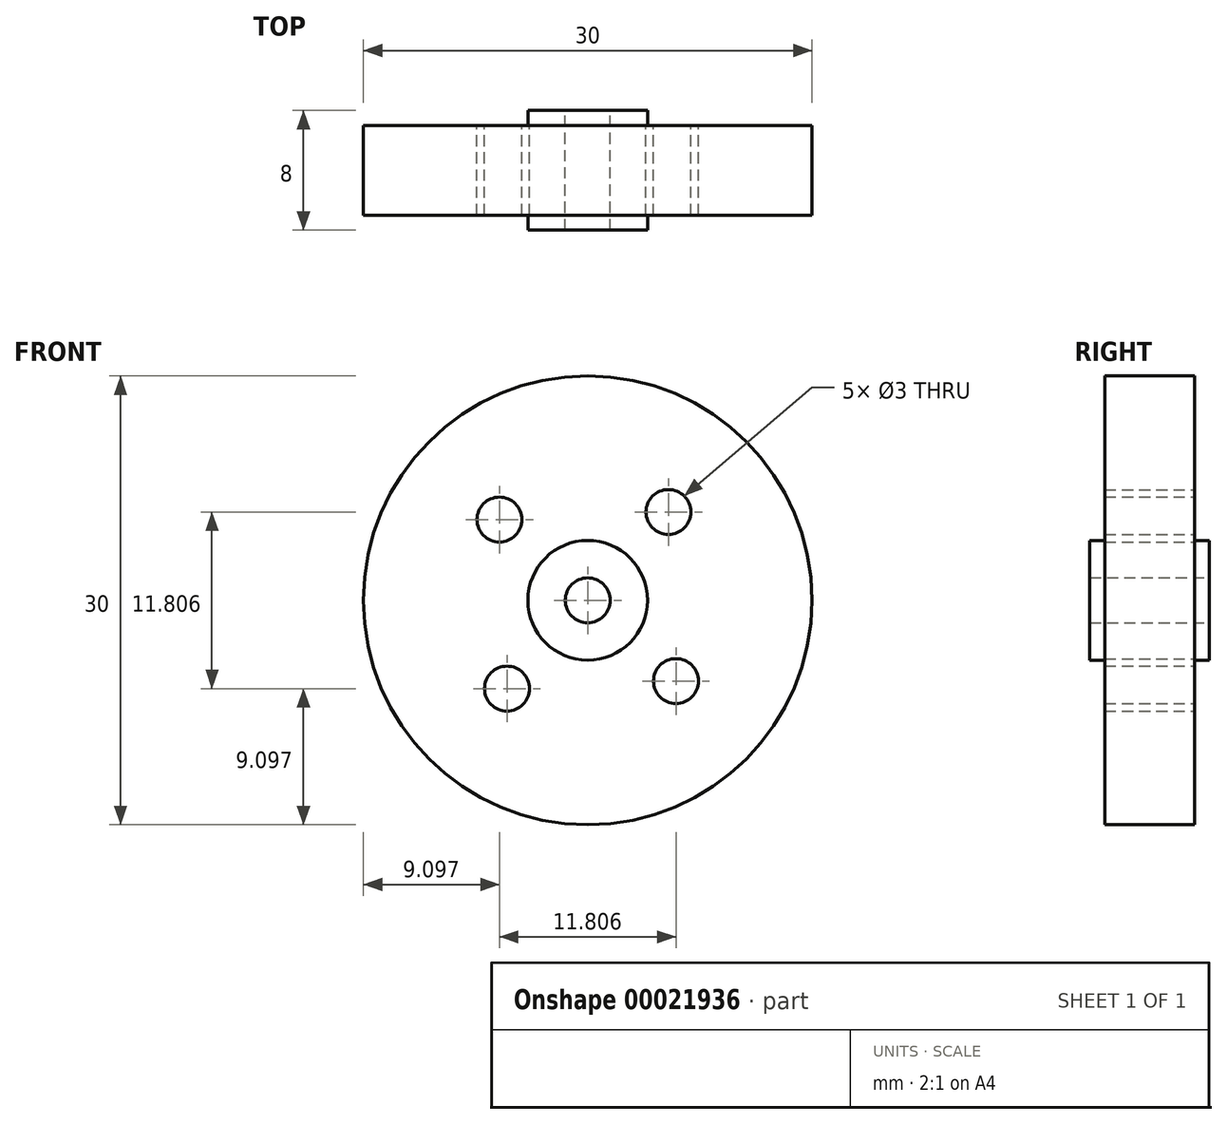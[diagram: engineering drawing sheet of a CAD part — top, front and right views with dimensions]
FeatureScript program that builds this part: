
annotation { "Feature Type Name" : "Feature", "Feature Type Description" : "" }
export const myFeature = defineFeature(function(context is Context, id is Id, definition is map)
    precondition{}
    {
        {
            var Q0;
            Q0=qCreatedBy(makeId("Front.planeOp"),FACE);
            var sketch = newSketch(context, id + "F0", { "sketchPlane" : qUnion([Q0])});
            skCircle(sketch, "E0", {"center": v(0, 0) * mm, "radius": 15 * mm});
            skCircle(sketch, "E1", {"center": v(0, 0) * mm, "radius": 1.5 * mm});
            skCircle(sketch, "E2", {"center": v(0, 0) * mm, "radius": 4 * mm});
            skCircle(sketch, "E3", {"center": v(-5.9, 5.4) * mm, "radius": 1.5 * mm});
            skCircle(sketch, "E4.1.0", {"center": v(-5.4, -5.9) * mm, "radius": 1.5 * mm});
            skCircle(sketch, "E4.2.0", {"center": v(5.9, -5.4) * mm, "radius": 1.5 * mm});
            skCircle(sketch, "E4.3.0", {"center": v(5.4, 5.9) * mm, "radius": 1.5 * mm});
            skSolve(sketch);
        }
        {
            var Q0;
            Q0=makeQuery(id+"F0.imprint","IMPRINT",FACE,{"disambiguationData":[TD([[makeQuery(id+"F0.imprint","IMPRINT",EDGE,{"derivedFrom":sQuery(id+"F0.wireOp",EDGE,"E0")}),1.0]])]});
            extrude(context, id + "F1", {"entities" : qUnion([Q0]), "endBound" : BoundingType.SYMMETRIC, "depth" : 6 * mm});
        }
        {
            var Q0;
            Q0=makeQuery(id+"F0.imprint","IMPRINT",FACE,{"disambiguationData":[TD([[makeQuery(id+"F0.imprint","IMPRINT",EDGE,{"derivedFrom":sQuery(id+"F0.wireOp",EDGE,"E1")}),-1.0]])]});
            extrude(context, id + "F2", {"entities" : qUnion([Q0]), "operationType" : NewBodyOperationType.ADD, "endBound" : BoundingType.SYMMETRIC, "depth" : 8 * mm});
        }
    });
